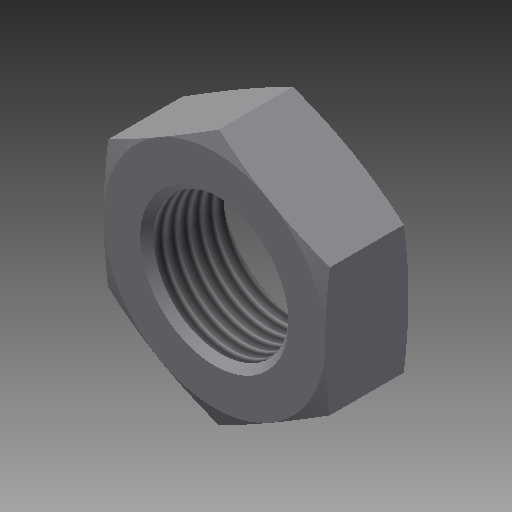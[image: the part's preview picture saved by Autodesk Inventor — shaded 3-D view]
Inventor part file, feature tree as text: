
AUTODESK INVENTOR PART (.ipt)
format: ipt  version: 2019 (Build 230136000, 136)  size: 186,880 bytes
history: native  units: in
note: dims shown in document units (in); Inventor stores cm internally (conversion verified against a paired STEP export)
features: other x70, sketch x3, revolve x2, extrude x1, thread x1
ambient origin geometry x8: Origin, YZ Plane, XZ Plane, XY Plane, X Axis, Y Axis, Z Axis, Center Point
bodies: Solid1 (feature_tree)
feature tree (77):
  sketch  "Sketch_8"  dims[d0=360.0deg d1=0.42in d2=0.0in]
  sketch  "Sketch_10"  dims[d3=360.0deg d4=0.3523in d5=0.0in]
  revolve  "Revolution1"  [1 undecoded]
  extrude  "Extrusion1"  Depth=0.3523in TaperAngle=0.0deg
  revolve  "Revolution2"  [1 undecoded]
  thread  "Thread1"  [1 undecoded]
  other  "NUT_XY"
  other  "NUT_YZ"
  other  "NUT_ZX"
  other  "NUT_X"
  other  "NUT_Y"
  other  "NUT_Z"
  other  "NUT_Center"
  other  "a1_XY"
  other  "a1_YZ"
  other  "a1_ZX"
  other  "a1_X"
  other  "a1_Y"
  other  "a1_Z"
  other  "a1_Center"
  other  "a2_XY"
  other  "a2_YZ"
  other  "a2_ZX"
  other  "a2_X"
  other  "a2_Y"
  other  "a2_Z"
  other  "a2_Center"
  other  "b1_XY"
  other  "b1_YZ"
  other  "b1_ZX"
  other  "b1_X"
  other  "b1_Y"
  other  "b1_Z"
  other  "b1_Center"
  other  "b2_XY"
  other  "b2_YZ"
  other  "b2_ZX"
  other  "b2_X"
  other  "b2_Y"
  other  "b2_Z"
  other  "b2_Center"
  other  "e_XY"
  other  "e_YZ"
  other  "e_ZX"
  other  "e_X"
  other  "e_Y"
  other  "e_Z"
  other  "e_Center"
  other  "ol1_XY"
  other  "ol1_YZ"
  other  "ol1_ZX"
  other  "ol1_X"
  other  "ol1_Y"
  other  "ol1_Z"
  other  "ol1_Center"
  other  "ol2_XY"
  other  "ol2_YZ"
  other  "ol2_ZX"
  other  "ol2_X"
  other  "ol2_Y"
  other  "ol2_Z"
  other  "ol2_Center"
  other  "th1_XY"
  other  "th1_YZ"
  other  "th1_ZX"
  other  "th1_X"
  other  "th1_Y"
  other  "th1_Z"
  other  "th1_Center"
  other  "th2_XY"
  other  "th2_YZ"
  other  "th2_ZX"
  other  "th2_X"
  other  "th2_Y"
  other  "th2_Z"
  other  "th2_Center"
  sketch  "Sketch_11"  dims[d6=0.0in d7=0.0in d8=0.0in]
note: 3 required parameter values undecoded (feature->parameter linkage not recoverable at this tier; creation-order binding heuristic only, values carry confidence <= 0.55)